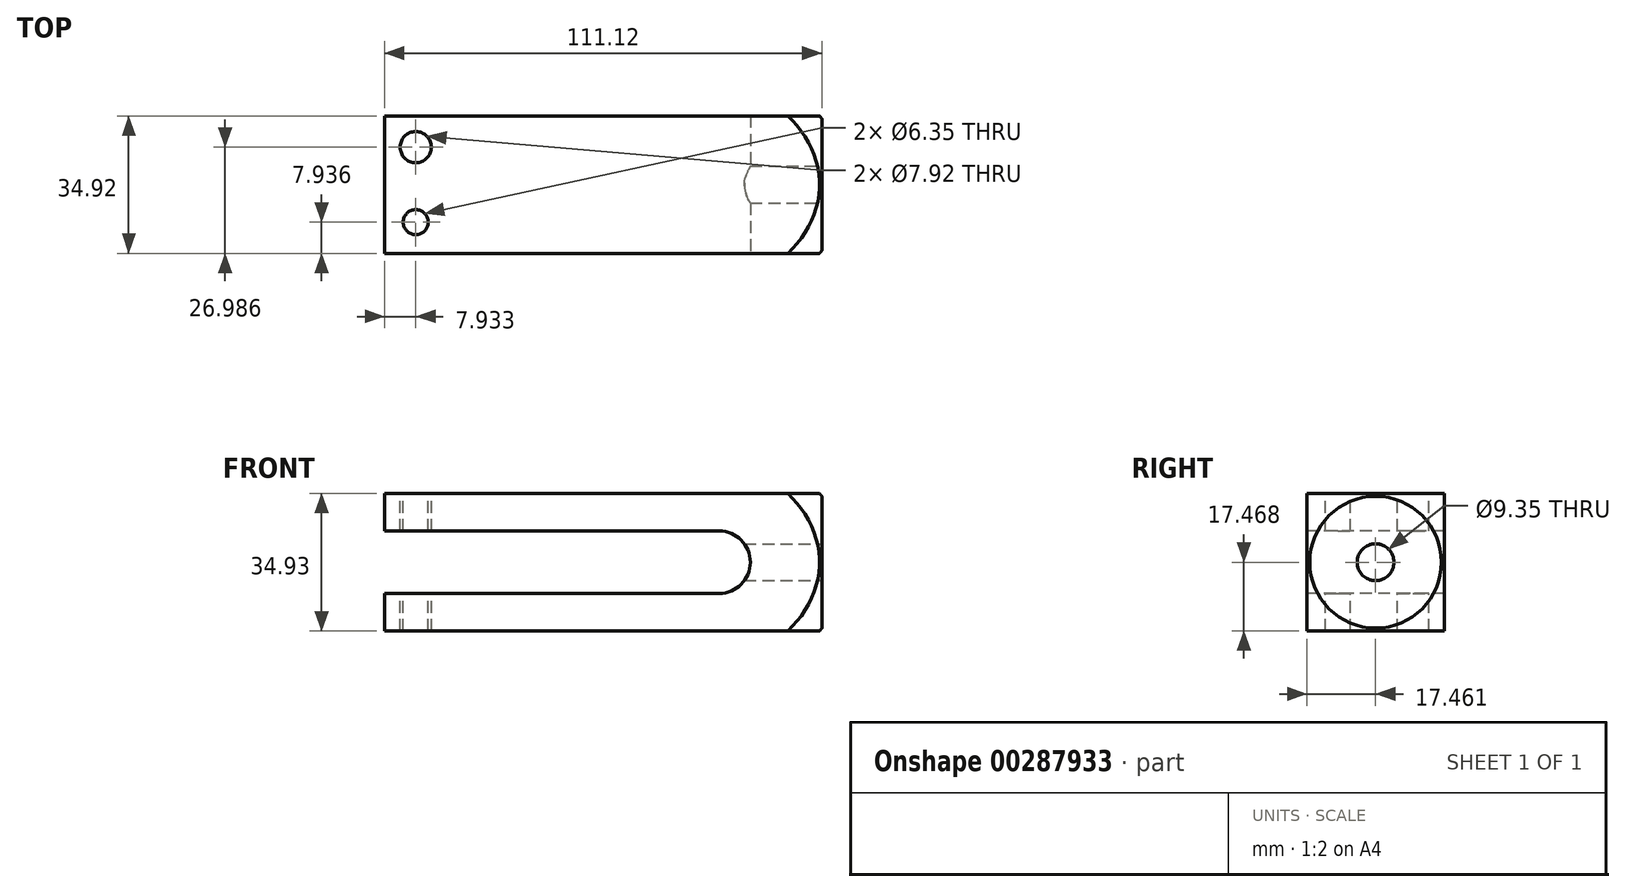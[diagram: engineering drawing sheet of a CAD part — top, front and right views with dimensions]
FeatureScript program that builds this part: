
annotation { "Feature Type Name" : "Feature", "Feature Type Description" : "" }
export const myFeature = defineFeature(function(context is Context, id is Id, definition is map)
    precondition{}
    {
        {
            var Q0;
            Q0=qCreatedBy(makeId("Top.planeOp"),FACE);
            var sketch = newSketch(context, id + "F0", { "sketchPlane" : qUnion([Q0])});
            skLineSegment(sketch, "E0.bottom", {"start": v(-65.03, 56.43) * mm, "end": v(46.1, 56.43) * mm});
            skLineSegment(sketch, "E0.top", {"start": v(-65.03, 21.5) * mm, "end": v(46.1, 21.5) * mm});
            skLineSegment(sketch, "E0.left", {"start": v(-65.03, 56.43) * mm, "end": v(-65.03, 21.5) * mm});
            skLineSegment(sketch, "E0.right", {"start": v(46.1, 56.43) * mm, "end": v(46.1, 21.5) * mm});
            skSolve(sketch);
        }
        {
            var Q0;
            Q0=makeQuery(id+"F0.imprint","IMPRINT",FACE,{"disambiguationData":[TD([[makeQuery(id+"F0.imprint","IMPRINT",EDGE,{"derivedFrom":sQuery(id+"F0.wireOp",EDGE,"E0.bottom")}),-1.0]])]});
            extrude(context, id + "F1", {"entities" : qUnion([Q0]), "oppositeDirection" : true, "depth" : 34.92 * mm, "offsetDistance" : 25.4 * mm});
        }
        {
            var Q0;
            Q0=makeQuery(id+"F1.opExtrude","SWEPT_FACE",FACE,{"disambiguationData":[OSD([sQuery(id+"F0.wireOp",EDGE,"E0.top")])]});
            var sketch = newSketch(context, id + "F2", { "sketchPlane" : qUnion([Q0])});
            skLineSegment(sketch, "E1", {"start": v(-65.03, -9.53) * mm, "end": v(19.98, -9.52) * mm});
            skLineSegment(sketch, "E2", {"start": v(19.98, -9.52) * mm, "end": v(19.98, -25.4) * mm});
            skLineSegment(sketch, "E3", {"start": v(19.98, -25.4) * mm, "end": v(-65.03, -25.4) * mm});
            skArc(sketch, "E4", {"start": v(19.98, -25.4) * mm, "mid": v(27.92, -17.46) * mm, "end": v(19.98, -9.52) * mm});
            skSolve(sketch);
        }
        {
            var Q0;
            {var subQ0=sQuery(id+"F2.wireOp",EDGE,"E1");Q0=makeQuery(id+"F2.imprint","IMPRINT",FACE,{"disambiguationData":[TD([[makeQuery(id+"F2.imprint","IMPRINT",EDGE,{"derivedFrom":subQ0}),-1.0]])]});}
            var Q1;
            Q1=makeQuery(id+"F2.imprint","IMPRINT",FACE,{"disambiguationData":[TD([[makeQuery(id+"F2.imprint","IMPRINT",EDGE,{"derivedFrom":sQuery(id+"F2.wireOp",EDGE,"E2")}),1.0]])]});
            extrude(context, id + "F3", {"entities" : qUnion([Q0, Q1]), "operationType" : NewBodyOperationType.REMOVE, "oppositeDirection" : true, "depth" : 50.8 * mm, "offsetDistance" : 25.4 * mm});
        }
        {
            var Q0;
            Q0=makeQuery(id+"F1.opExtrude","CAP_FACE",FACE,{"disambiguationData":[OSD([sQuery(id+"F0.wireOp",EDGE,"E0.bottom"),sQuery(id+"F0.wireOp",EDGE,"E0.top"),sQuery(id+"F0.wireOp",EDGE,"E0.left"),sQuery(id+"F0.wireOp",EDGE,"E0.right")])],"isStart":false});
            var Q1;
            Q1=makeQuery(id+"F1.opExtrude","CAP_FACE",FACE,{"disambiguationData":[OSD([sQuery(id+"F0.wireOp",EDGE,"E0.bottom"),sQuery(id+"F0.wireOp",EDGE,"E0.top"),sQuery(id+"F0.wireOp",EDGE,"E0.left"),sQuery(id+"F0.wireOp",EDGE,"E0.right")])],"isStart":true});
            cPlane(context, id + "F4", {"entities" : qUnion([Q0, Q1]), "cplaneType" : CPlaneType.MID_PLANE, "offset" : 25.4 * mm, "width" : 152.4 * mm, "height" : 152.4 * mm});
        }
        {
            var Q0;
            Q0=qCreatedBy(id+"F4.planeOp",FACE);
            var sketch = newSketch(context, id + "F5", { "sketchPlane" : qUnion([Q0])});
            skLineSegment(sketch, "E5", {"start": v(-82.75, -38.97) * mm, "end": v(87.54, -38.97) * mm});
            skLineSegment(sketch, "E6", {"start": v(34.98, -56.43) * mm, "end": v(46.1, -56.43) * mm, "construction": true});
            skLineSegment(sketch, "E7", {"start": v(46.1, -56.43) * mm, "end": v(46.1, -38.97) * mm, "construction": true});
            skPoint(sketch, "E8", {"position": v(46.1, -55.64) * mm});
            skArc(sketch, "E9", {"start": v(34.98, -65.2) * mm, "mid": v(47.27, -54.15) * mm, "end": v(53.82, -38.97) * mm});
            skLineSegment(sketch, "E10", {"start": v(34.98, -65.2) * mm, "end": v(53.82, -65.2) * mm});
            skLineSegment(sketch, "E11", {"start": v(53.82, -65.2) * mm, "end": v(53.82, -38.97) * mm});
            skSolve(sketch);
        }
        {
            var Q0;
            Q0=makeQuery(id+"F5.imprint","IMPRINT",FACE,{"disambiguationData":[TD([[makeQuery(id+"F5.imprint","IMPRINT",EDGE,{"derivedFrom":sQuery(id+"F5.wireOp",EDGE,"E9")}),-1.0]])]});
            var Q1;
            Q1=sQuery(id+"F5.wireOp",EDGE,"E5");
            revolve(context, id + "F6", {"operationType" : NewBodyOperationType.REMOVE, "entities" : qUnion([Q0]), "axis" : qUnion([Q1]), "revolveType" : RevolveType.ONE_DIRECTION, "oppositeDirection" : true, "angle" : 360 * degree});
        }
        {
            var Q0;
            Q0=makeQuery(id+"F1.opExtrude","SWEPT_FACE",FACE,{"disambiguationData":[OSD([sQuery(id+"F0.wireOp",EDGE,"E0.right")])]});
            var sketch = newSketch(context, id + "F7", { "sketchPlane" : qUnion([Q0])});
            skPoint(sketch, "E12", {"position": v(38.97, -17.46) * mm});
            skSolve(sketch);
        }
        {
            var Q0;
            Q0=sQuery(id+"F7.wireOp",VERTEX,"E12");
            var Q1;
            Q1=makeQuery(id+"F1.opExtrude","SWEPT_BODY",BODY,{"disambiguationData":[OSD([sQuery(id+"F0.wireOp",EDGE,"E0.bottom"),sQuery(id+"F0.wireOp",EDGE,"E0.top"),sQuery(id+"F0.wireOp",EDGE,"E0.left"),sQuery(id+"F0.wireOp",EDGE,"E0.right")])]});
            hole(context, id + "F8", {"style" : HoleStyle.SIMPLE, "endStyle" : HoleEndStyle.THROUGH, "standardTappedOrClearance" : lookupTablePath({ "standard" : "ANSI", "engagement" : "75%", "pitch" : "14 tpi", "size" : "7/16", "type" : "Tapped" }), "standardBlindInLast" : lookupTablePath({ "standard" : "ANSI", "engagement" : "75%", "pitch" : "14 tpi", "size" : "7/16", "type" : "Tapped" }), "holeDiameter" : 9.35 * mm, "majorDiameter" : 11.1 * mm, "showTappedDepth" : true, "isTappedThrough" : true, "tappedDepth" : 21.59 * mm, "tapClearance" : 3, "locations" : qUnion([Q0]), "scope" : qUnion([Q1])});
        }
        {
            var Q0;
            Q0=makeQuery(id+"F5.imprint","IMPRINT",FACE,{"disambiguationData":[TD([[makeQuery(id+"F5.imprint","IMPRINT",EDGE,{"derivedFrom":sQuery(id+"F5.wireOp",EDGE,"E9")}),-1.0]])]});
            extrude(context, id + "F9", {"entities" : qUnion([Q0]), "operationType" : NewBodyOperationType.REMOVE, "oppositeDirection" : true, "depth" : 25.4 * mm, "offsetDistance" : 25.4 * mm});
        }
        {
            var Q0;
            Q0=makeQuery(id+"F1.opExtrude","CAP_FACE",FACE,{"disambiguationData":[OSD([sQuery(id+"F0.wireOp",EDGE,"E0.bottom"),sQuery(id+"F0.wireOp",EDGE,"E0.top"),sQuery(id+"F0.wireOp",EDGE,"E0.left"),sQuery(id+"F0.wireOp",EDGE,"E0.right")])],"isStart":true});
            var sketch = newSketch(context, id + "F10", { "sketchPlane" : qUnion([Q0])});
            skPoint(sketch, "E13", {"position": v(-57.1, 29.45) * mm});
            skPoint(sketch, "E14", {"position": v(-57.1, 48.5) * mm});
            skSolve(sketch);
        }
        {
            var Q0;
            Q0=sQuery(id+"F10.wireOp",VERTEX,"E13");
            var Q1;
            Q1=makeQuery(id+"F1.opExtrude","SWEPT_BODY",BODY,{"disambiguationData":[OSD([sQuery(id+"F0.wireOp",EDGE,"E0.bottom"),sQuery(id+"F0.wireOp",EDGE,"E0.top"),sQuery(id+"F0.wireOp",EDGE,"E0.left"),sQuery(id+"F0.wireOp",EDGE,"E0.right")])]});
            hole(context, id + "F11", {"style" : HoleStyle.SIMPLE, "endStyle" : HoleEndStyle.THROUGH, "holeDiameter" : 6.35 * mm, "majorDiameter" : 11.1 * mm, "isTappedThrough" : true, "tappedDepth" : 21.59 * mm, "tapClearance" : 3, "locations" : qUnion([Q0]), "scope" : qUnion([Q1])});
        }
        {
            var Q0;
            Q0=sQuery(id+"F10.wireOp",VERTEX,"E14");
            var Q1;
            Q1=makeQuery(id+"F1.opExtrude","SWEPT_BODY",BODY,{"disambiguationData":[OSD([sQuery(id+"F0.wireOp",EDGE,"E0.bottom"),sQuery(id+"F0.wireOp",EDGE,"E0.top"),sQuery(id+"F0.wireOp",EDGE,"E0.left"),sQuery(id+"F0.wireOp",EDGE,"E0.right")])]});
            hole(context, id + "F12", {"style" : HoleStyle.SIMPLE, "endStyle" : HoleEndStyle.THROUGH, "holeDiameter" : 7.92 * mm, "majorDiameter" : 7.94 * mm, "isTappedThrough" : true, "tappedDepth" : 21.59 * mm, "tapClearance" : 3, "locations" : qUnion([Q0]), "scope" : qUnion([Q1])});
        }
    });
